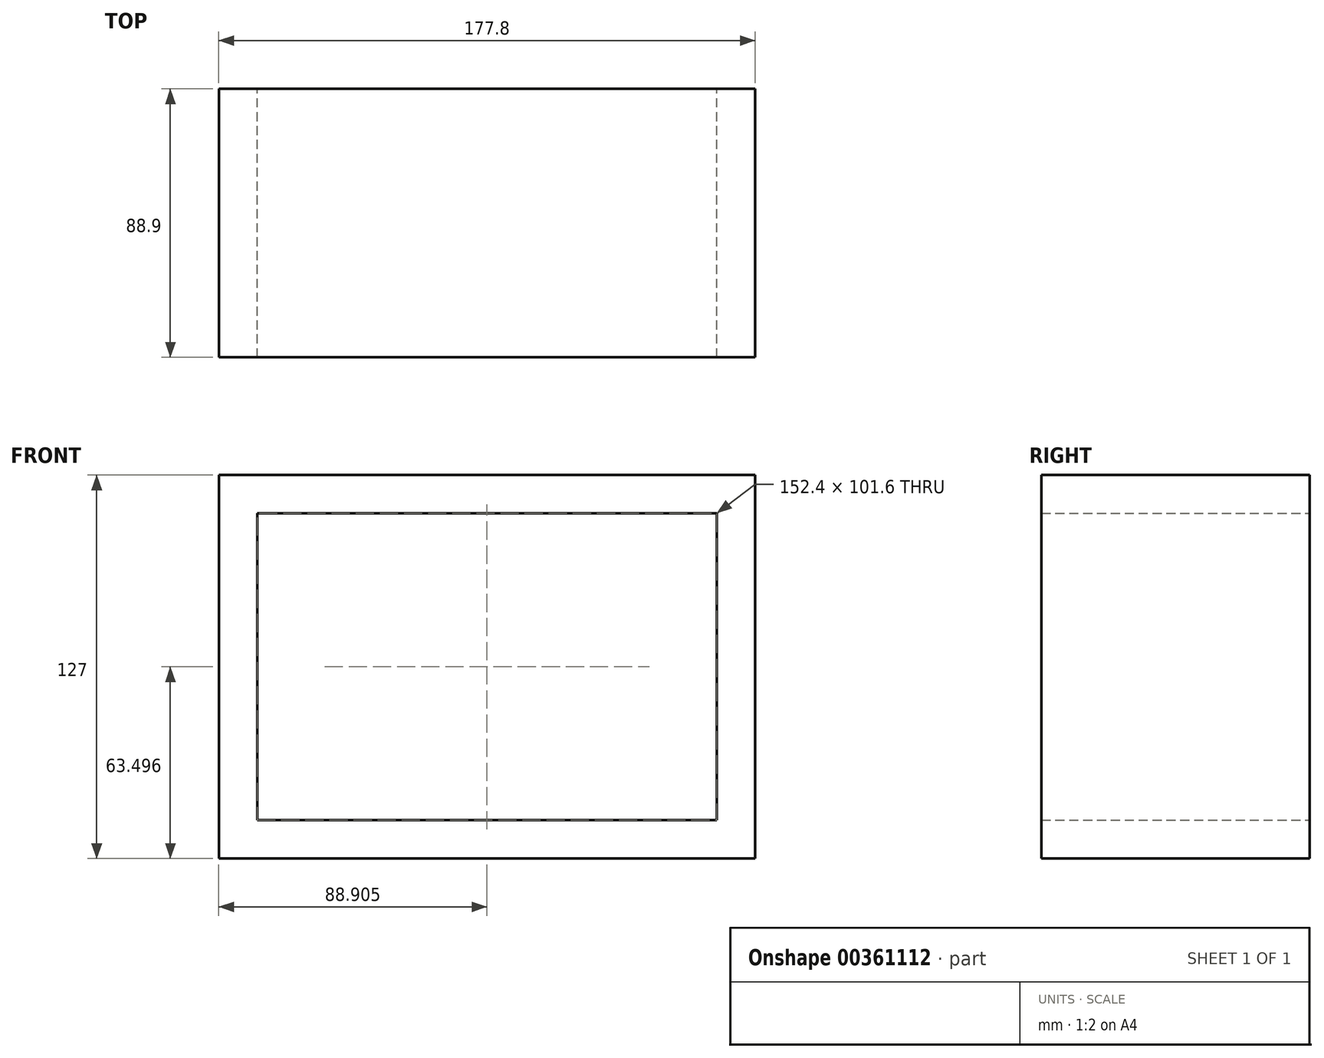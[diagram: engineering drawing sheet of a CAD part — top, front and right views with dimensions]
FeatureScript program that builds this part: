
annotation { "Feature Type Name" : "Feature", "Feature Type Description" : "" }
export const myFeature = defineFeature(function(context is Context, id is Id, definition is map)
    precondition{}
    {
        {
            var Q0;
            Q0=qCreatedBy(makeId("Front.planeOp"),FACE);
            var sketch = newSketch(context, id + "F0", { "sketchPlane" : qUnion([Q0])});
            skLineSegment(sketch, "E0.bottom", {"start": v(-93.3, 34.05) * mm, "end": v(84.5, 34.05) * mm});
            skLineSegment(sketch, "E0.top", {"start": v(-93.3, -92.95) * mm, "end": v(84.5, -92.95) * mm});
            skLineSegment(sketch, "E0.left", {"start": v(-93.3, 34.05) * mm, "end": v(-93.3, -92.95) * mm});
            skLineSegment(sketch, "E0.right", {"start": v(84.5, 34.05) * mm, "end": v(84.5, -92.95) * mm});
            skLineSegment(sketch, "E1.bottom", {"start": v(-80.6, 21.35) * mm, "end": v(71.8, 21.35) * mm});
            skLineSegment(sketch, "E1.top", {"start": v(-80.6, -80.25) * mm, "end": v(71.8, -80.25) * mm});
            skLineSegment(sketch, "E1.left", {"start": v(-80.6, 21.35) * mm, "end": v(-80.6, -80.25) * mm});
            skLineSegment(sketch, "E1.right", {"start": v(71.8, 21.35) * mm, "end": v(71.8, -80.25) * mm});
            skSolve(sketch);
        }
        {
            var Q0;
            Q0 = qSketchRegion(id + "F0", true);
            extrude(context, id + "F1", {"entities" : qUnion([Q0]), "depth" : 88.9 * mm});
        }
    });
